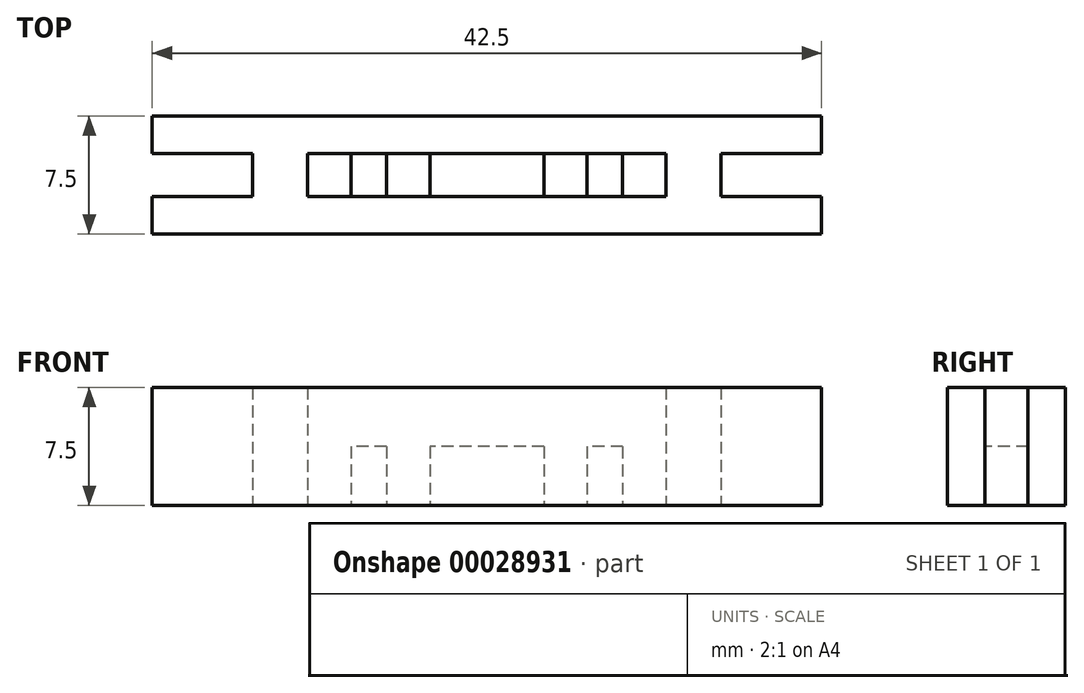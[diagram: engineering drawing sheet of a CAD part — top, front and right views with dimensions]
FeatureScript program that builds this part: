
annotation { "Feature Type Name" : "Feature", "Feature Type Description" : "" }
export const myFeature = defineFeature(function(context is Context, id is Id, definition is map)
    precondition{}
    {
        {
            var Q0;
            Q0=qCreatedBy(makeId("Top.planeOp"),FACE);
            var sketch = newSketch(context, id + "F0", { "sketchPlane" : qUnion([Q0])});
            skLineSegment(sketch, "E0.bottom", {"start": v(0, 0) * mm, "end": v(42.5, 0) * mm});
            skLineSegment(sketch, "E0.top", {"start": v(0, 7.5) * mm, "end": v(42.5, 7.5) * mm});
            skLineSegment(sketch, "E0.left", {"start": v(0, 0) * mm, "end": v(0, 7.5) * mm});
            skLineSegment(sketch, "E0.right", {"start": v(42.5, 0) * mm, "end": v(42.5, 7.5) * mm});
            skLineSegment(sketch, "E1.bottom", {"start": v(0, 5.13) * mm, "end": v(42.5, 5.13) * mm});
            skLineSegment(sketch, "E1.top", {"start": v(0, 2.38) * mm, "end": v(42.5, 2.38) * mm});
            skLineSegment(sketch, "E1.left", {"start": v(0, 5.13) * mm, "end": v(0, 2.38) * mm});
            skLineSegment(sketch, "E1.right", {"start": v(42.5, 5.13) * mm, "end": v(42.5, 2.38) * mm});
            skLineSegment(sketch, "E2", {"start": v(2.37, 5.13) * mm, "end": v(2.37, 2.38) * mm});
            skLineSegment(sketch, "E3", {"start": v(21.25, 7.5) * mm, "end": v(21.25, 0) * mm, "construction": true});
            skLineSegment(sketch, "E4", {"start": v(6.38, 5.13) * mm, "end": v(6.38, 2.37) * mm});
            skLineSegment(sketch, "E5", {"start": v(9.88, 5.13) * mm, "end": v(9.88, 2.37) * mm});
            skLineSegment(sketch, "E6", {"start": v(12.62, 5.13) * mm, "end": v(12.62, 2.37) * mm});
            skLineSegment(sketch, "E7", {"start": v(14.88, 5.13) * mm, "end": v(14.88, 2.38) * mm});
            skLineSegment(sketch, "E8", {"start": v(17.62, 5.13) * mm, "end": v(17.62, 2.38) * mm});
            skLineSegment(sketch, "E9.MirrorCS", {"start": v(24.88, 5.13) * mm, "end": v(24.88, 2.38) * mm});
            skLineSegment(sketch, "E10.MirrorCS", {"start": v(27.63, 5.13) * mm, "end": v(27.63, 2.38) * mm});
            skLineSegment(sketch, "E11.MirrorCS", {"start": v(29.88, 5.13) * mm, "end": v(29.88, 2.37) * mm});
            skLineSegment(sketch, "E12.MirrorCS", {"start": v(32.62, 5.13) * mm, "end": v(32.62, 2.37) * mm});
            skLineSegment(sketch, "E13.MirrorCS", {"start": v(36.13, 5.13) * mm, "end": v(36.13, 2.37) * mm});
            skLineSegment(sketch, "E14.MirrorCS", {"start": v(40.12, 5.13) * mm, "end": v(40.12, 2.38) * mm});
            skSolve(sketch);
        }
        {
            var Q0;
            {var subQ17=sQuery(id+"F0.wireOp",EDGE,"E0.top");Q0=makeQuery(id+"F0.imprint","IMPRINT",FACE,{"disambiguationData":[TD([[makeQuery(id+"F0.imprint","IMPRINT",EDGE,{"derivedFrom":subQ17}),-1.0]])]});}
            var Q1;
            {var subQ1=sQuery(id+"F0.wireOp",EDGE,"E1.left");Q1=makeQuery(id+"F0.imprint","IMPRINT",FACE,{"disambiguationData":[TD([[makeQuery(id+"F0.imprint","IMPRINT",EDGE,{"derivedFrom":subQ1}),1.0]])]});}
            var Q2;
            {var subQ17=sQuery(id+"F0.wireOp",EDGE,"E0.bottom");Q2=makeQuery(id+"F0.imprint","IMPRINT",FACE,{"disambiguationData":[TD([[makeQuery(id+"F0.imprint","IMPRINT",EDGE,{"derivedFrom":subQ17}),1.0]])]});}
            var Q3;
            {var subQ1=sQuery(id+"F0.wireOp",EDGE,"E4");Q3=makeQuery(id+"F0.imprint","IMPRINT",FACE,{"disambiguationData":[TD([[makeQuery(id+"F0.imprint","IMPRINT",EDGE,{"derivedFrom":subQ1}),1.0]])]});}
            var Q4;
            {var subQ1=sQuery(id+"F0.wireOp",EDGE,"E6");Q4=makeQuery(id+"F0.imprint","IMPRINT",FACE,{"disambiguationData":[TD([[makeQuery(id+"F0.imprint","IMPRINT",EDGE,{"derivedFrom":subQ1}),1.0]])]});}
            var Q5;
            {var subQ1=sQuery(id+"F0.wireOp",EDGE,"E8");Q5=makeQuery(id+"F0.imprint","IMPRINT",FACE,{"disambiguationData":[TD([[makeQuery(id+"F0.imprint","IMPRINT",EDGE,{"derivedFrom":subQ1}),1.0]])]});}
            var Q6;
            {var subQ1=sQuery(id+"F0.wireOp",EDGE,"E10.MirrorCS");Q6=makeQuery(id+"F0.imprint","IMPRINT",FACE,{"disambiguationData":[TD([[makeQuery(id+"F0.imprint","IMPRINT",EDGE,{"derivedFrom":subQ1}),1.0]])]});}
            var Q7;
            {var subQ1=sQuery(id+"F0.wireOp",EDGE,"E12.MirrorCS");Q7=makeQuery(id+"F0.imprint","IMPRINT",FACE,{"disambiguationData":[TD([[makeQuery(id+"F0.imprint","IMPRINT",EDGE,{"derivedFrom":subQ1}),1.0]])]});}
            var Q8;
            {var subQ1=sQuery(id+"F0.wireOp",EDGE,"E1.right");Q8=makeQuery(id+"F0.imprint","IMPRINT",FACE,{"disambiguationData":[TD([[makeQuery(id+"F0.imprint","IMPRINT",EDGE,{"derivedFrom":subQ1}),-1.0]])]});}
            extrude(context, id + "F1", {"entities" : qUnion([Q0, Q1, Q2, Q3, Q4, Q5, Q6, Q7, Q8]), "depth" : 3.75 * mm});
        }
        {
            var Q0;
            {var subQ17=sQuery(id+"F0.wireOp",EDGE,"E0.top");Q0=makeQuery(id+"F0.imprint","IMPRINT",FACE,{"disambiguationData":[TD([[makeQuery(id+"F0.imprint","IMPRINT",EDGE,{"derivedFrom":subQ17}),-1.0]])]});}
            var Q1;
            {var subQ17=sQuery(id+"F0.wireOp",EDGE,"E0.bottom");Q1=makeQuery(id+"F0.imprint","IMPRINT",FACE,{"disambiguationData":[TD([[makeQuery(id+"F0.imprint","IMPRINT",EDGE,{"derivedFrom":subQ17}),1.0]])]});}
            var Q2;
            {var subQ1=sQuery(id+"F0.wireOp",EDGE,"E4");Q2=makeQuery(id+"F0.imprint","IMPRINT",FACE,{"disambiguationData":[TD([[makeQuery(id+"F0.imprint","IMPRINT",EDGE,{"derivedFrom":subQ1}),1.0]])]});}
            var Q3;
            {var subQ1=sQuery(id+"F0.wireOp",EDGE,"E12.MirrorCS");Q3=makeQuery(id+"F0.imprint","IMPRINT",FACE,{"disambiguationData":[TD([[makeQuery(id+"F0.imprint","IMPRINT",EDGE,{"derivedFrom":subQ1}),1.0]])]});}
            extrude(context, id + "F2", {"entities" : qUnion([Q0, Q1, Q2, Q3]), "operationType" : NewBodyOperationType.ADD, "depth" : 7.5 * mm});
        }
    });
